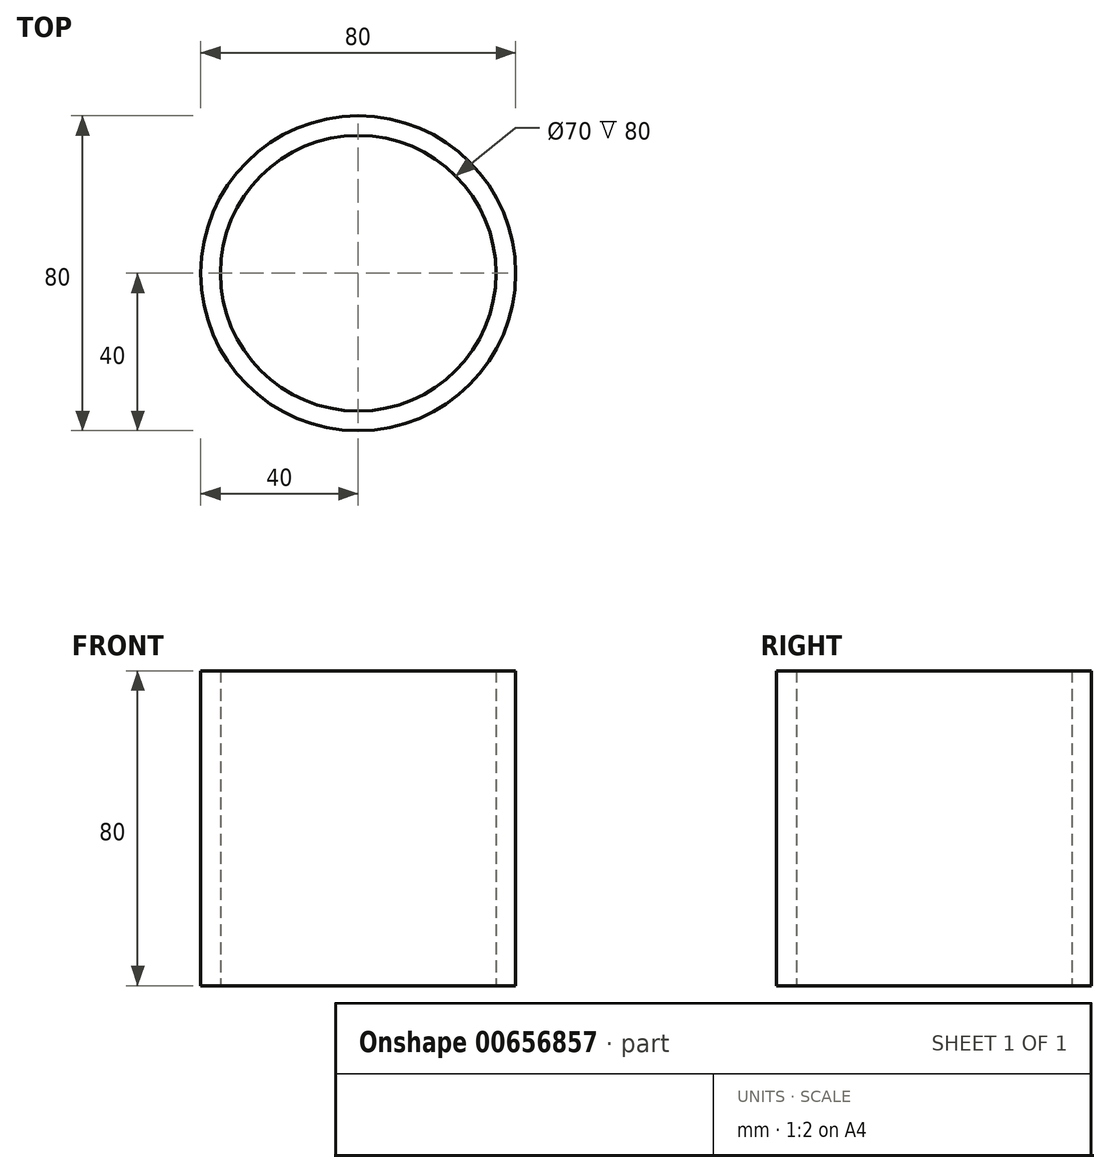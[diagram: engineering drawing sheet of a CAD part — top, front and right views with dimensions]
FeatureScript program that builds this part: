
annotation { "Feature Type Name" : "Feature", "Feature Type Description" : "" }
export const myFeature = defineFeature(function(context is Context, id is Id, definition is map)
    precondition{}
    {
        {
            var Q0;
            Q0=qCreatedBy(makeId("Top.planeOp"),FACE);
            var sketch = newSketch(context, id + "F0", { "sketchPlane" : qUnion([Q0])});
            skCircle(sketch, "E0", {"center": v(0, 0) * mm, "radius": 40 * mm});
            skCircle(sketch, "E1", {"center": v(0, 0) * mm, "radius": 35 * mm});
            skSolve(sketch);
        }
        {
            var Q0;
            Q0 = qSketchRegion(id + "F0", true);
            extrude(context, id + "F1", {"entities" : qUnion([Q0]), "endBound" : BoundingType.SYMMETRIC, "depth" : 80 * mm, "offsetDistance" : 25 * mm});
        }
    });
